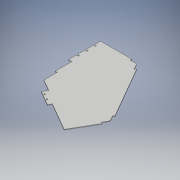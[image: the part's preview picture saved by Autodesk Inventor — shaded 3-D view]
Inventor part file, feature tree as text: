
AUTODESK INVENTOR PART (.ipt)
format: ipt  version: 2019.4 (Build 234330000, 330)  size: 222,208 bytes
history: native  units: mm
features: sketch x7, extrude x5, fillet x1
ambient origin geometry x8: Origin, YZ Plane, XZ Plane, XY Plane, X Axis, Y Axis, Z Axis, Center Point
bodies: Solid1 (feature_tree)
feature tree (13):
  extrude  "Extrusion1"  Depth=303.0mm
  extrude  "Extrusion2"  Depth=16.0mm
  extrude  "Extrusion3"  Depth=30.0mm TaperAngle=360.0deg
  extrude  "Extrusion4"  Depth=151.5mm
  extrude  "Extrusion5"  Depth=152.5mm
  sketch  "Sketch6"  dims[d15=3.0mm d16=0.0mm]
  sketch  "Sketch7"  dims[d17=35.0mm d18=8.0mm d19=35.0mm d20=8.0mm d21=35.0mm d22=8.0mm d23=35.0mm d24=120.0deg d25=8.0mm d26=3.0mm d27=0.0mm d28=145.0mm d29=30.0deg d30=35.0mm d31=145.0mm d32=90.0deg d33=35.0mm d34=3.0mm d35=0.0mm d36=40.0mm d37=5.5mm d38=30.0mm d40=40.0mm d41=10.0mm d43=10.0mm d45=1.0mm d46=6.5mm d47=30.0mm d48=30.0mm d49=5.5mm d50=5.5mm d51=3.0mm d52=0.0mm d53=7.0mm d54=352.0mm d55=450.0mm d56=351.0mm d57=447.0mm d58=10.0mm]
  fillet  "Fillet1"  Radius=17.0mm
  sketch  "Sketch1"  dims[d0=303.0mm d1=303.0mm]
  sketch  "Sketch2"  dims[d2=8.0mm d3=16.0mm]
  sketch  "Sketch3"  dims[d4=5.0mm d5=30.0mm d7=360.0deg]
  sketch  "Sketch4"  dims[d9=3.0mm d10=0.0mm d11=151.5mm]
  sketch  "Sketch5"  dims[d12=16.0mm d13=152.5mm d14=17.0mm]
